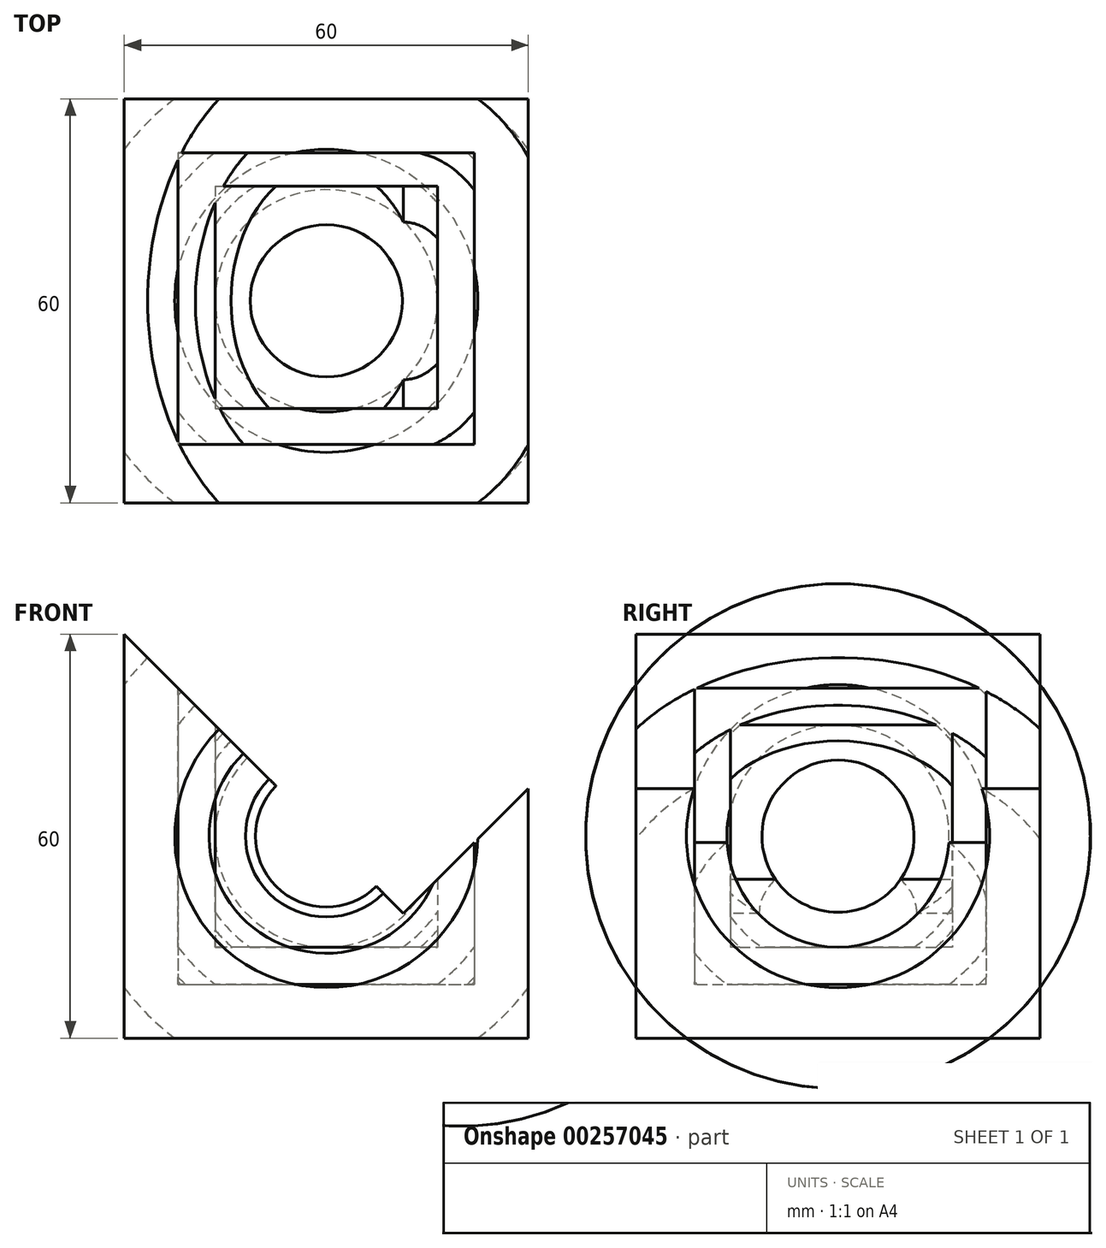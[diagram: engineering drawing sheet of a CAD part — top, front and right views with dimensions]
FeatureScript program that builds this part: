
annotation { "Feature Type Name" : "Feature", "Feature Type Description" : "" }
export const myFeature = defineFeature(function(context is Context, id is Id, definition is map)
    precondition{}
    {
        {
            var Q0;
            Q0=qCreatedBy(makeId("Front.planeOp"),FACE);
            var sketch = newSketch(context, id + "F0", { "sketchPlane" : qUnion([Q0])});
            skLineSegment(sketch, "E0.bottom", {"start": v(0, 0) * mm, "end": v(60, 0) * mm});
            skLineSegment(sketch, "E0.top", {"start": v(0, 60) * mm, "end": v(60, 60) * mm});
            skLineSegment(sketch, "E0.left", {"start": v(0, 0) * mm, "end": v(0, 60) * mm});
            skLineSegment(sketch, "E0.right", {"start": v(60, 0) * mm, "end": v(60, 60) * mm});
            skSolve(sketch);
        }
        {
            var Q0;
            Q0 = qSketchRegion(id + "F0", true);
            extrude(context, id + "F1", {"entities" : qUnion([Q0]), "depth" : 60 * mm});
        }
        {
            var Q0;
            Q0=makeQuery(id+"F1.opExtrude","CAP_FACE",FACE,{"disambiguationData":[OSD([sQuery(id+"F0.wireOp",EDGE,"E0.bottom"),sQuery(id+"F0.wireOp",EDGE,"E0.top"),sQuery(id+"F0.wireOp",EDGE,"E0.left"),sQuery(id+"F0.wireOp",EDGE,"E0.right")])],"isStart":false});
            var Q1;
            Q1=makeQuery(id+"F1.opExtrude","CAP_FACE",FACE,{"disambiguationData":[OSD([sQuery(id+"F0.wireOp",EDGE,"E0.bottom"),sQuery(id+"F0.wireOp",EDGE,"E0.top"),sQuery(id+"F0.wireOp",EDGE,"E0.left"),sQuery(id+"F0.wireOp",EDGE,"E0.right")])],"isStart":true});
            cPlane(context, id + "F2", {"entities" : qUnion([Q0, Q1]), "cplaneType" : CPlaneType.MID_PLANE, "offset" : 25 * mm, "width" : 150 * mm, "height" : 150 * mm});
        }
        {
            var Q0;
            Q0=qCreatedBy(id+"F2.planeOp",FACE);
            var sketch = newSketch(context, id + "F3", { "sketchPlane" : qUnion([Q0])});
            skLineSegment(sketch, "E1", {"start": v(0, 0) * mm, "end": v(60, 60) * mm, "construction": true});
            skCircle(sketch, "E2", {"center": v(30, 30) * mm, "radius": 37.5 * mm, "construction": true});
            skLineSegment(sketch, "E3", {"start": v(30, 30) * mm, "end": v(30, 67.5) * mm});
            skLineSegment(sketch, "E4", {"start": v(30, 30) * mm, "end": v(30, -7.5) * mm});
            skArc(sketch, "E5", {"start": v(30, 67.5) * mm, "mid": v(-7.5, 30) * mm, "end": v(30, -7.5) * mm});
            skSolve(sketch);
        }
        {
            var Q0;
            Q0 = qSketchRegion(id + "F3", true);
            var Q1;
            Q1=sQuery(id+"F3.wireOp",EDGE,"E3");
            revolve(context, id + "F4", {"operationType" : NewBodyOperationType.REMOVE, "entities" : qUnion([Q0]), "axis" : qUnion([Q1]), "revolveType" : RevolveType.FULL, "oppositeDirection" : true});
        }
        {
            var Q0;
            Q0=makeQuery(id+"F1.opExtrude","SWEPT_FACE",FACE,{"disambiguationData":[OSD([sQuery(id+"F0.wireOp",EDGE,"E0.left")])]});
            var Q1;
            Q1=makeQuery(id+"F1.opExtrude","SWEPT_FACE",FACE,{"disambiguationData":[OSD([sQuery(id+"F0.wireOp",EDGE,"E0.right")])]});
            cPlane(context, id + "F5", {"entities" : qUnion([Q0, Q1]), "cplaneType" : CPlaneType.MID_PLANE, "offset" : 25 * mm, "width" : 150 * mm, "height" : 150 * mm});
        }
        {
            var Q0;
            Q0=makeQuery(id+"F1.opExtrude","CAP_FACE",FACE,{"disambiguationData":[OSD([sQuery(id+"F0.wireOp",EDGE,"E0.bottom"),sQuery(id+"F0.wireOp",EDGE,"E0.top"),sQuery(id+"F0.wireOp",EDGE,"E0.left"),sQuery(id+"F0.wireOp",EDGE,"E0.right")])],"isStart":false});
            cPlane(context, id + "F6", {"entities" : qUnion([Q0]), "cplaneType" : CPlaneType.OFFSET, "offset" : 4 * mm, "oppositeDirection" : true, "width" : 150 * mm, "height" : 150 * mm});
        }
        {
            var Q0;
            Q0=makeQuery(id+"F1.opExtrude","CAP_VERTEX",VERTEX,{"disambiguationData":[OSD([sQuery(id+"F0.wireOp",EDGE,"E0.bottom"),sQuery(id+"F0.wireOp",EDGE,"E0.right")])],"isStart":true});
            var Q1;
            Q1=makeQuery(id+"F1.opExtrude","CAP_VERTEX",VERTEX,{"disambiguationData":[OSD([sQuery(id+"F0.wireOp",EDGE,"E0.top"),sQuery(id+"F0.wireOp",EDGE,"E0.left")])],"isStart":true});
            var Q2;
            Q2=makeQuery(id+"F1.opExtrude","CAP_VERTEX",VERTEX,{"disambiguationData":[OSD([sQuery(id+"F0.wireOp",EDGE,"E0.bottom"),sQuery(id+"F0.wireOp",EDGE,"E0.right")])],"isStart":false});
            cPlane(context, id + "F7", {"entities" : qUnion([Q0, Q1, Q2]), "cplaneType" : CPlaneType.THREE_POINT, "offset" : 25 * mm, "width" : 150 * mm, "height" : 150 * mm});
        }
        {
            var Q0;
            Q0=qCreatedBy(id+"F7.planeOp",FACE);
            var sketch = newSketch(context, id + "F8", { "sketchPlane" : qUnion([Q0])});
            skPoint(sketch, "E6", {"position": v(30.62, 8.35) * mm});
            skPoint(sketch, "E7", {"position": v(-30.62, 51.65) * mm});
            skLineSegment(sketch, "E8", {"start": v(42.43, 0) * mm, "end": v(30.62, 8.35) * mm});
            skLineSegment(sketch, "E9", {"start": v(-30.62, 51.65) * mm, "end": v(-42.43, 60) * mm});
            skSolve(sketch);
        }
        {
            var Q0;
            Q0=makeQuery(id+"F1.opExtrude","CAP_FACE",FACE,{"disambiguationData":[OSD([sQuery(id+"F0.wireOp",EDGE,"E0.bottom"),sQuery(id+"F0.wireOp",EDGE,"E0.top"),sQuery(id+"F0.wireOp",EDGE,"E0.left"),sQuery(id+"F0.wireOp",EDGE,"E0.right")])],"isStart":true});
            cPlane(context, id + "F9", {"entities" : qUnion([Q0]), "cplaneType" : CPlaneType.OFFSET, "offset" : 8 * mm, "oppositeDirection" : true, "width" : 150 * mm, "height" : 150 * mm});
        }
        {
            var Q0;
            Q0=qCreatedBy(id+"F9.planeOp",FACE);
            var sketch = newSketch(context, id + "F10", { "sketchPlane" : qUnion([Q0])});
            skLineSegment(sketch, "E10.bottom", {"start": v(-8, 52) * mm, "end": v(-52, 52) * mm});
            skLineSegment(sketch, "E10.top", {"start": v(-8, 8) * mm, "end": v(-52, 8) * mm});
            skLineSegment(sketch, "E10.left", {"start": v(-8, 52) * mm, "end": v(-8, 8) * mm});
            skLineSegment(sketch, "E10.right", {"start": v(-52, 52) * mm, "end": v(-52, 8) * mm});
            skPoint(sketch, "E10.middle", {"position": v(-30, 30) * mm});
            skSolve(sketch);
        }
        {
            var Q0;
            Q0 = qSketchRegion(id + "F10", true);
            extrude(context, id + "F11", {"entities" : qUnion([Q0]), "operationType" : NewBodyOperationType.ADD, "oppositeDirection" : true, "depth" : (60 - 8.35 * 2) * mm});
        }
        {
            var Q0;
            Q0=qCreatedBy(id+"F5.planeOp",FACE);
            var sketch = newSketch(context, id + "F12", { "sketchPlane" : qUnion([Q0])});
            skCircle(sketch, "E11", {"center": v(30, 30) * mm, "radius": 27.5 * mm, "construction": true});
            skLineSegment(sketch, "E12", {"start": v(30, 30) * mm, "end": v(2.5, 30) * mm});
            skLineSegment(sketch, "E13", {"start": v(30, 30) * mm, "end": v(57.5, 30) * mm});
            skArc(sketch, "E14", {"start": v(57.5, 30) * mm, "mid": v(30, 57.5) * mm, "end": v(2.5, 30) * mm});
            skSolve(sketch);
        }
        {
            var Q0;
            Q0 = qSketchRegion(id + "F12", true);
            var Q1;
            Q1=sQuery(id+"F12.wireOp",EDGE,"E12");
            revolve(context, id + "F13", {"operationType" : NewBodyOperationType.REMOVE, "entities" : qUnion([Q0]), "axis" : qUnion([Q1]), "revolveType" : RevolveType.FULL, "oppositeDirection" : true});
        }
        {
            var Q0;
            Q0=qCreatedBy(id+"F9.planeOp",FACE);
            cPlane(context, id + "F14", {"entities" : qUnion([Q0]), "cplaneType" : CPlaneType.OFFSET, "offset" : 5 * mm, "oppositeDirection" : true, "width" : 150 * mm, "height" : 150 * mm});
        }
        {
            var Q0;
            Q0=qCreatedBy(id+"F14.planeOp",FACE);
            var sketch = newSketch(context, id + "F15", { "sketchPlane" : qUnion([Q0])});
            skLineSegment(sketch, "E15.bottom", {"start": v(-46.5, 46.5) * mm, "end": v(-13.5, 46.5) * mm});
            skLineSegment(sketch, "E15.top", {"start": v(-46.5, 13.5) * mm, "end": v(-13.5, 13.5) * mm});
            skLineSegment(sketch, "E15.left", {"start": v(-46.5, 46.5) * mm, "end": v(-46.5, 13.5) * mm});
            skLineSegment(sketch, "E15.right", {"start": v(-13.5, 46.5) * mm, "end": v(-13.5, 13.5) * mm});
            skPoint(sketch, "E15.middle", {"position": v(-30, 30) * mm});
            skSolve(sketch);
        }
        {
            var Q0;
            Q0 = qSketchRegion(id + "F15", true);
            extrude(context, id + "F16", {"entities" : qUnion([Q0]), "operationType" : NewBodyOperationType.ADD, "oppositeDirection" : true, "depth" : 33 * mm});
        }
        {
            var Q0;
            Q0=qCreatedBy(id+"F5.planeOp",FACE);
            var sketch = newSketch(context, id + "F17", { "sketchPlane" : qUnion([Q0])});
            skCircle(sketch, "E16", {"center": v(30, 30) * mm, "radius": 20 * mm, "construction": true});
            skLineSegment(sketch, "E17", {"start": v(30, 30) * mm, "end": v(50, 30) * mm});
            skLineSegment(sketch, "E18", {"start": v(30, 30) * mm, "end": v(10, 30) * mm});
            skArc(sketch, "E19", {"start": v(10, 30) * mm, "mid": v(30, 10) * mm, "end": v(50, 30) * mm});
            skSolve(sketch);
        }
        {
            var Q0;
            Q0 = qSketchRegion(id + "F17", true);
            var Q1;
            Q1=sQuery(id+"F17.wireOp",EDGE,"E17");
            revolve(context, id + "F18", {"operationType" : NewBodyOperationType.REMOVE, "entities" : qUnion([Q0]), "axis" : qUnion([Q1]), "revolveType" : RevolveType.FULL, "oppositeDirection" : true});
        }
        {
            var Q0;
            Q0=qCreatedBy(id+"F7.planeOp",FACE);
            var sketch = newSketch(context, id + "F19", { "sketchPlane" : qUnion([Q0])});
            skLineSegment(sketch, "E20.bottom", {"start": v(-54.86, -16.22) * mm, "end": v(68.96, -16.22) * mm});
            skLineSegment(sketch, "E20.top", {"start": v(-54.86, 86.25) * mm, "end": v(68.96, 86.25) * mm});
            skLineSegment(sketch, "E20.left", {"start": v(-54.86, -16.22) * mm, "end": v(-54.86, 86.25) * mm});
            skLineSegment(sketch, "E20.right", {"start": v(68.96, -16.22) * mm, "end": v(68.96, 86.25) * mm});
            skSolve(sketch);
        }
        {
            var Q0;
            Q0 = qSketchRegion(id + "F19", true);
            extrude(context, id + "F20", {"entities" : qUnion([Q0]), "operationType" : NewBodyOperationType.REMOVE, "endBound" : BoundingType.THROUGH_ALL, "oppositeDirection" : true, "depth" : 25 * mm});
        }
    });
